# Revit family: svetilnik_alfresco_strit-premier_dtu-27-af_i_dtu-34-af
name_source: partatom
category: Lighting Fixtures
revit_build: Autodesk Revit 2016 (Build: 20150506_1715(x64)
units: mm (PartAtom-declared; Revit-internal decimal feet)

## family parameters
Always vertical = Yes
Cut with Voids When Loaded = No
Light Source = Yes
Part Type = Normal
Room Calculation Point = No
Round Connector Dimension = Use Diameter
Shared = No
Work Plane-Based = No

## types (2) — shared parameters
ADSK_Единица измерения = шт
ADSK_Классификация нагрузок = Освещение
ADSK_Количество фаз = 2
ADSK_Количество фаз числовое = 2
ADSK_Коэффициент мощности = 0.97
ADSK_Напряжение = 220 V
ADSK_Номинальная мощность = 50 W
ADSK_Полная мощность = 52 VA
ADSK_Ток = 0 A
ADSK_Энергоэффективность = 120 lm/W
Apparent Load = 52 VA
Color Filter = 16777215
Dimming Lamp Color Temperature Shift = <None>
Emit Shape Visible in Rendering = No
IP Class = IP 65
Manufacturer = ALFRESCO
Tilt Angle = 90.00°
URL = http://www.allfresco.ru
Блок аварийного питания = No
Класс Защиты = 1
Класс пожароопасности = F (светильники предназначены для установки непосредственно на поверхность из нормально воспламеняемых матеоиалов)
Климатическая зона = У1
Материал опоры = Сталь, окрашенная, черная
Область использования = Ландшафт, коттедж.поселки,микрорайоны,АЗС, автостоянки
Световой поток = 6000 lm
Температура эксплуатации = -35 +40
Тип КСС = Sym
Тип ПРА = -
Тип продукции = LED-светильник
Цветовая температура = 3000-5500

## per-type parameters (varying)
| type | ADSK_Артикул | ADSK_Масса | ADSK_Модель | ADSK_Наименование | ADSK_Размер_Высота | ADSK_Размер_Длина | ADSK_Размер_Ширина | Emit from Circle Diameter | Photometric Web File | Высота источника света | Высота нижней части | Сечение по фланцу | Тип ИС |
| Стрит-Премьер ДТУ-27-AF-50Вт-3,6 | ДТУ271 | 30 | Стрит-Премьер ДТУ-27-AF | Светодиодный светильник Стрит-Премьер ДТУ-27-AF-50Вт-3,6 | 3600 mm  [stored 11.811 ft] | 108 mm  [stored 0.354331 ft] | 108 mm  [stored 0.354331 ft] | 108 mm  [stored 0.354331 ft] | ДТУ-27-AF StreetPremier50w.ies | 450 mm  [stored 1.47638 ft] | 3000 mm  [stored 9.84252 ft] | 240 mm  [stored 0.787402 ft] | LED-светодиоды |
| Стрит-Премьер ДТУ-34-AF-50Вт-5,0 | ДТУ341 | 56 | Стрит-Премьер ДТУ-34-AF | Светодиодный светильник Стрит-Премьер ДТУ-34-AF-50Вт-5,0 | 5000 mm  [stored 16.4042 ft] | 133 mm  [stored 0.436352 ft] | 133 mm  [stored 0.436352 ft] | 133 mm  [stored 0.436352 ft] | ДТУ-34-AF StreetPremier50w.ies | 1300 mm  [stored 4.26509 ft] | 3550 mm  [stored 11.647 ft] | 290 mm  [stored 0.951444 ft] | LED-СОВ |

note: [stored X ft] marks values corroborated as IEEE doubles in the binary element streams (Revit-internal decimal feet)
